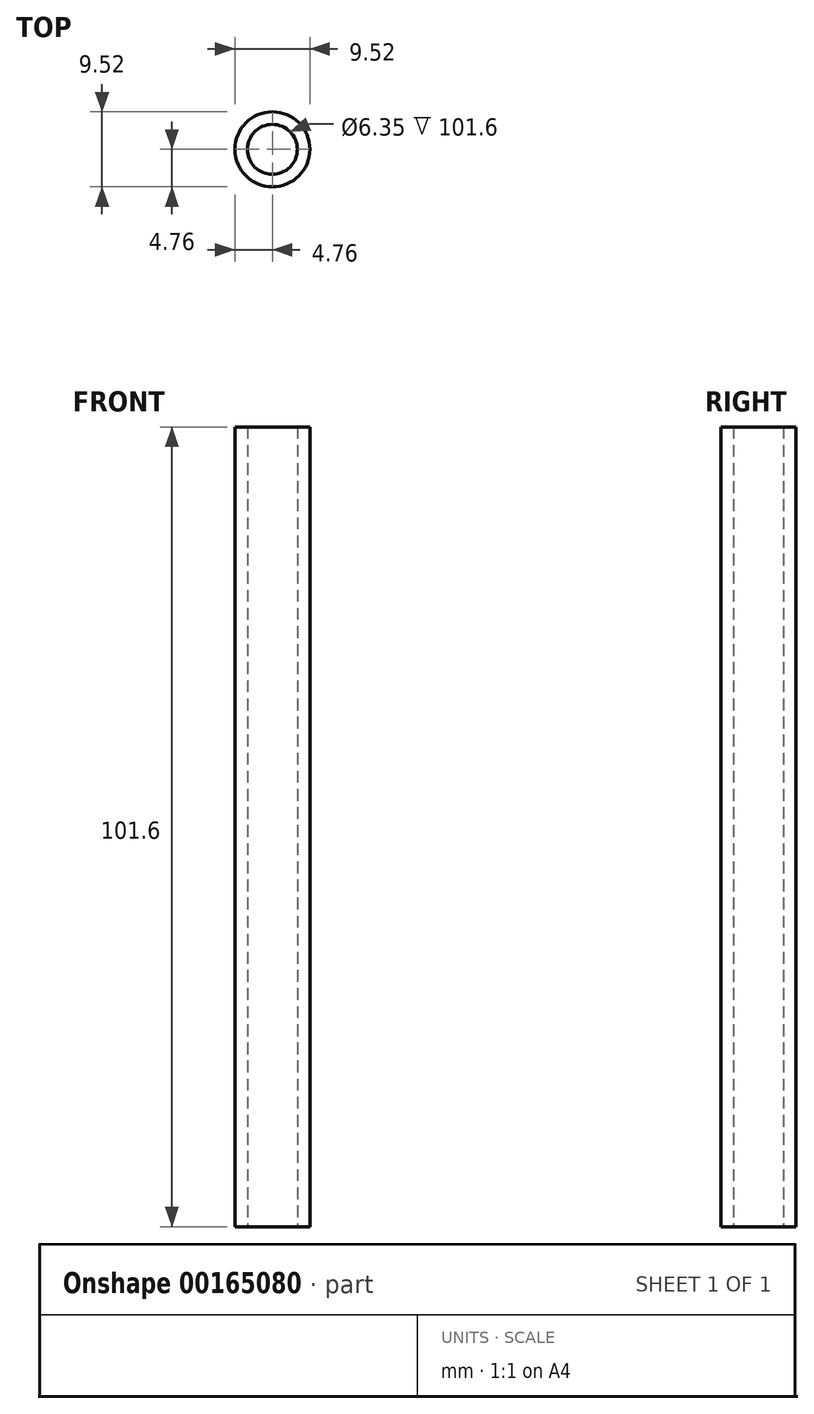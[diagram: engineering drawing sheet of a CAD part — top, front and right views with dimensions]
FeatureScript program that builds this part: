
annotation { "Feature Type Name" : "Feature", "Feature Type Description" : "" }
export const myFeature = defineFeature(function(context is Context, id is Id, definition is map)
    precondition{}
    {
        {
            var Q0;
            Q0=qCreatedBy(makeId("Top.planeOp"),FACE);
            var sketch = newSketch(context, id + "F0", { "sketchPlane" : qUnion([Q0])});
            skCircle(sketch, "E0", {"center": v(0, 0) * mm, "radius": 3.18 * mm});
            skCircle(sketch, "E1", {"center": v(0, 0) * mm, "radius": 4.76 * mm});
            skSolve(sketch);
        }
        {
            var Q0;
            Q0=qSketchRegion(id+"F0",true);
            extrude(context, id + "F1", {"entities" : qUnion([Q0]), "depth" : 101.6 * mm});
        }
    });
